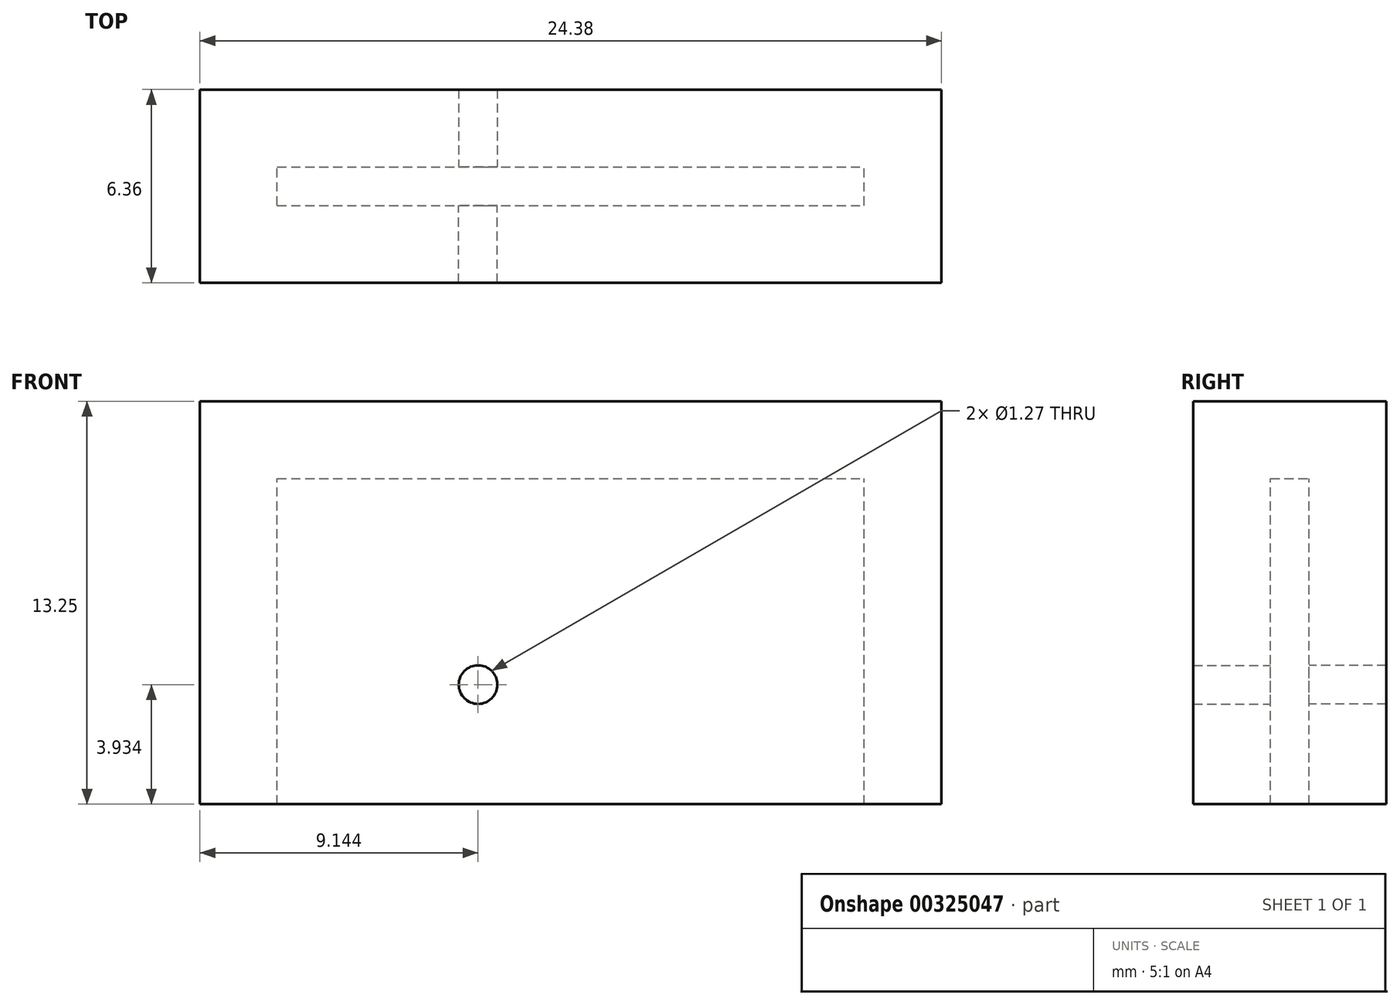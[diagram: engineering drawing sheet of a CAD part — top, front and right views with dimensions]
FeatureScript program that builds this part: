
annotation { "Feature Type Name" : "Feature", "Feature Type Description" : "" }
export const myFeature = defineFeature(function(context is Context, id is Id, definition is map)
    precondition{}
    {
        {
            var Q0;
            Q0=qCreatedBy(makeId("Front.planeOp"),FACE);
            var sketch = newSketch(context, id + "F0", { "sketchPlane" : qUnion([Q0])});
            skLineSegment(sketch, "E0.bottom", {"start": v(0, 33.52) * mm, "end": v(24.38, 33.52) * mm});
            skLineSegment(sketch, "E0.top", {"start": v(0, 46.77) * mm, "end": v(24.38, 46.77) * mm});
            skLineSegment(sketch, "E0.left", {"start": v(0, 33.52) * mm, "end": v(0, 46.77) * mm});
            skLineSegment(sketch, "E0.right", {"start": v(24.38, 33.52) * mm, "end": v(24.38, 46.77) * mm});
            skLineSegment(sketch, "E1", {"start": v(0, 33.52) * mm, "end": v(6.1, 33.52) * mm});
            skLineSegment(sketch, "E2", {"start": v(6.1, 33.52) * mm, "end": v(12.2, 33.52) * mm});
            skLineSegment(sketch, "E3", {"start": v(9.14, 33.52) * mm, "end": v(9.14, 37.45) * mm});
            skSolve(sketch);
        }
        {
            var Q0;
            Q0=makeQuery(id+"F0.imprint","IMPRINT",FACE,{"disambiguationData":[TD([[makeQuery(id+"F0.imprint","IMPRINT",EDGE,{"derivedFrom":sQuery(id+"F0.wireOp",EDGE,"E0.bottom")}),1.0]])]});
            extrude(context, id + "F1", {"entities" : qUnion([Q0]), "endBound" : BoundingType.SYMMETRIC, "depth" : 6.35 * mm});
        }
        {
            var Q0;
            Q0=makeQuery(id+"F1.opExtrude","SWEPT_FACE",FACE,{"disambiguationData":[OSD([sQuery(id+"F0.wireOp",EDGE,"E0.bottom"),sQuery(id+"F0.wireOp",EDGE,"E1"),sQuery(id+"F0.wireOp",EDGE,"E2")])]});
            shell(context, id + "F2", {"entities" : qUnion([Q0]), "thickness" : 2.54 * mm});
        }
        {
            var Q0;
            Q0=sQuery(id+"F0.wireOp",VERTEX,"E3.end");
            var Q1;
            Q1=makeQuery(id+"F1.opExtrude","SWEPT_BODY",BODY,{"disambiguationData":[OSD([sQuery(id+"F0.wireOp",EDGE,"E0.bottom"),sQuery(id+"F0.wireOp",EDGE,"E0.top"),sQuery(id+"F0.wireOp",EDGE,"E0.left"),sQuery(id+"F0.wireOp",EDGE,"E0.right"),sQuery(id+"F0.wireOp",EDGE,"E1"),sQuery(id+"F0.wireOp",EDGE,"E2")])]});
            hole(context, id + "F3", {"style" : HoleStyle.SIMPLE, "endStyle" : HoleEndStyle.THROUGH, "holeDiameter" : 1.27 * mm, "tappedDepth" : 12.7 * mm, "tapClearance" : 3, "locations" : qUnion([Q0]), "scope" : qUnion([Q1])});
        }
        {
            var Q0;
            Q0=sQuery(id+"F0.wireOp",VERTEX,"E3.end");
            var Q1;
            Q1=makeQuery(id+"F1.opExtrude","SWEPT_BODY",BODY,{"disambiguationData":[OSD([sQuery(id+"F0.wireOp",EDGE,"E0.bottom"),sQuery(id+"F0.wireOp",EDGE,"E0.top"),sQuery(id+"F0.wireOp",EDGE,"E0.left"),sQuery(id+"F0.wireOp",EDGE,"E0.right"),sQuery(id+"F0.wireOp",EDGE,"E1"),sQuery(id+"F0.wireOp",EDGE,"E2")])]});
            hole(context, id + "F4", {"style" : HoleStyle.SIMPLE, "endStyle" : HoleEndStyle.THROUGH, "oppositeDirection" : true, "holeDiameter" : 1.27 * mm, "tappedDepth" : 12.7 * mm, "tapClearance" : 3, "locations" : qUnion([Q0]), "scope" : qUnion([Q1])});
        }
    });
